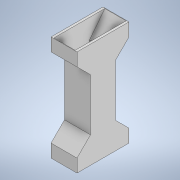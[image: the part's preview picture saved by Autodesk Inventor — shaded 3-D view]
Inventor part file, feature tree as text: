
AUTODESK INVENTOR PART (.ipt)
format: ipt  version: 2022 (Build 260153000, 153)  size: 182,272 bytes
history: native  units: mm
features: extrude x7, sketch x7, plane x2, mirror x1
ambient origin geometry x8: Origin, YZ Plane, XZ Plane, XY Plane, X Axis, Y Axis, Z Axis, Center Point
bodies: Solid1 (feature_tree)
feature tree (17):
  extrude  "Extrusion1"  Depth=80.0mm
  plane  "Work Plane1"
  extrude  "Extrusion2"  Depth=12.7mm
  extrude  "Extrusion3"  Depth=3.0mm
  extrude  "Extrusion4"  Depth=3.0mm
  extrude  "Extrusion5"  Depth=32.8mm TaperAngle=0.0deg
  extrude  "Extrusion6"  Depth=3.0mm TaperAngle=0.0deg
  extrude  "Extrusion7"  Depth=3.6mm
  plane  "Work Plane2"
  mirror  "Mirror1"
  sketch  "Sketch1"  dims[d0=34.0mm d1=80.0mm]
  sketch  "Sketch2"  dims[d2=30.0mm d3=0.0mm d4=12.7mm]
  sketch  "Sketch3"  dims[d5=12.7mm d6=3.0mm]
  sketch  "Sketch4"  dims[d7=0.75mm d8=3.0mm]
  sketch  "Sketch5"  dims[d9=0.75mm d10=32.8mm d11=0.0mm]
  sketch  "Sketch6"  dims[d12=3.0mm d13=0.0mm d14=3.0mm d15=0.0mm]
  sketch  "Sketch7"  dims[d16=10.0mm d17=10.0mm d18=10.0mm d19=0.0mm d20=0.0mm d21=3.6mm d22=76.2mm d23=0.0mm d24=45.0deg d25=0.0mm d26=0.0mm d27=-25.4mm]
